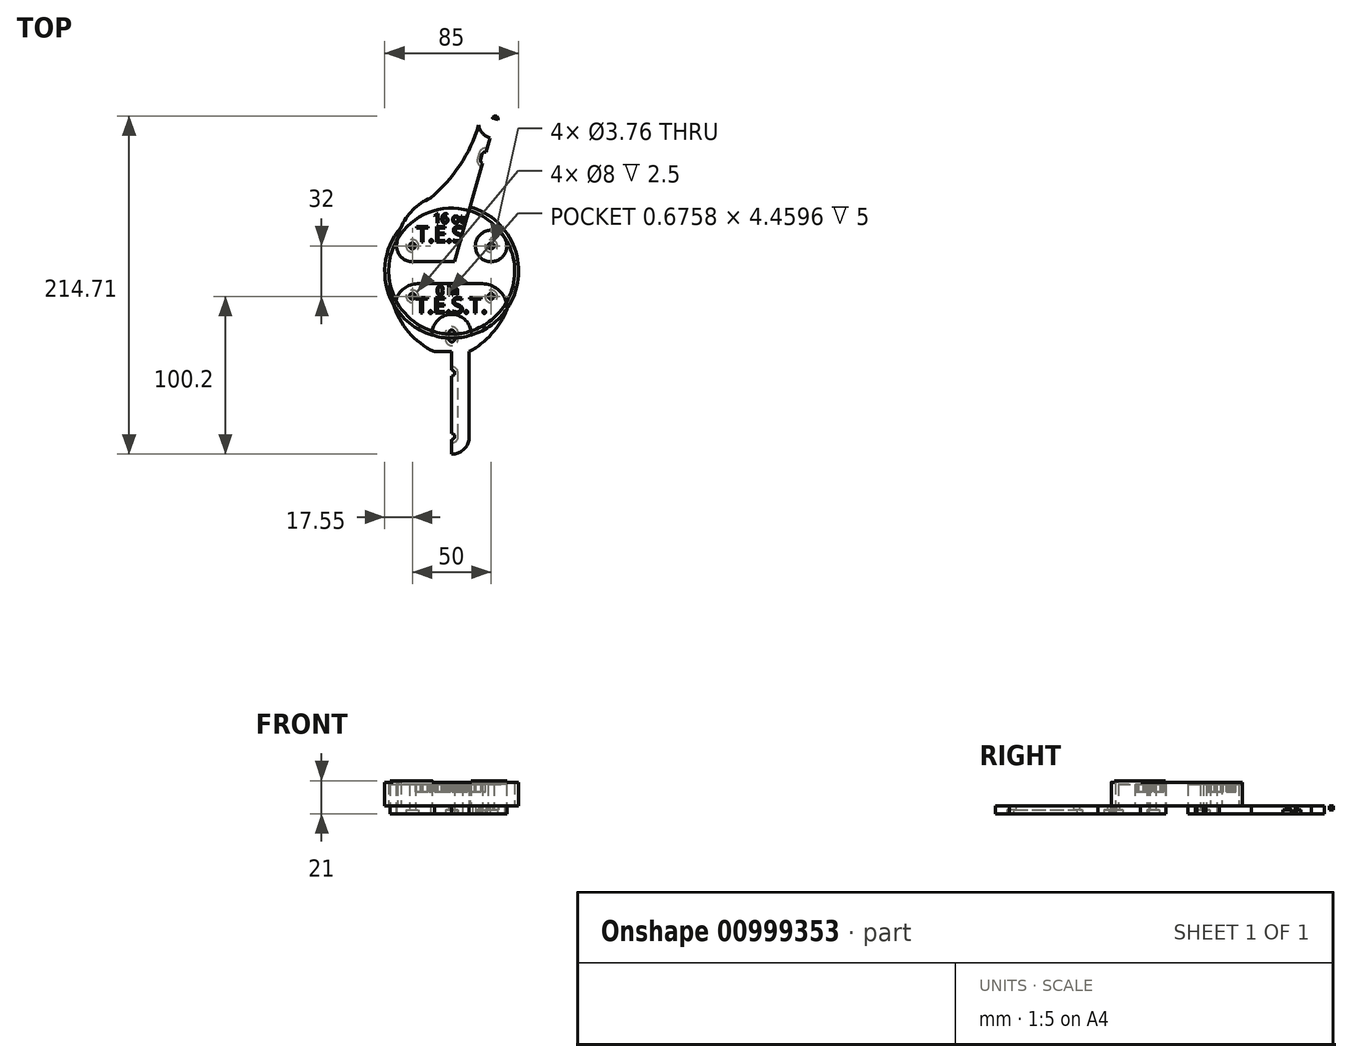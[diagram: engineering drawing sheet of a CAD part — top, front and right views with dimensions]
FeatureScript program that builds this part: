
annotation { "Feature Type Name" : "Feature", "Feature Type Description" : "" }
export const myFeature = defineFeature(function(context is Context, id is Id, definition is map)
    precondition{}
    {
        {
            var Q0;
            Q0=qCreatedBy(makeId("Top.planeOp"),FACE);
            var sketch = newSketch(context, id + "F0", { "sketchPlane" : qUnion([Q0])});
            skCircle(sketch, "E0", {"center": v(0.05, 0) * mm, "radius": 40 * mm});
            skLineSegment(sketch, "E1", {"start": v(0.05, 0) * mm, "end": v(0.05, -41.2) * mm});
            skLineSegment(sketch, "E2", {"start": v(0.05, -41.2) * mm, "end": v(0.05, -51.2) * mm});
            skLineSegment(sketch, "E3", {"start": v(0.05, -51.2) * mm, "end": v(0.05, -116.2) * mm});
            skLineSegment(sketch, "E4.bottom", {"start": v(6.4, -39.7) * mm, "end": v(-6.3, -39.7) * mm});
            skLineSegment(sketch, "E4.top", {"start": v(6.4, -42.7) * mm, "end": v(-6.3, -42.7) * mm});
            skLineSegment(sketch, "E4.left", {"start": v(6.4, -39.7) * mm, "end": v(6.4, -42.7) * mm});
            skLineSegment(sketch, "E4.right", {"start": v(-6.3, -39.7) * mm, "end": v(-6.3, -42.7) * mm});
            skPoint(sketch, "E4.middle", {"position": v(0.05, -41.2) * mm});
            skLineSegment(sketch, "E5", {"start": v(0.05, -51.2) * mm, "end": v(0.05, -83.7) * mm});
            skLineSegment(sketch, "E6.bottom", {"start": v(11.05, -51.2) * mm, "end": v(-10.95, -51.2) * mm});
            skLineSegment(sketch, "E6.top", {"start": v(11.05, -116.2) * mm, "end": v(-10.95, -116.2) * mm});
            skLineSegment(sketch, "E6.left", {"start": v(11.05, -51.2) * mm, "end": v(11.05, -107.3) * mm});
            skLineSegment(sketch, "E6.right", {"start": v(-10.95, -51.2) * mm, "end": v(-10.95, -116.2) * mm});
            skPoint(sketch, "E6.middle", {"position": v(0.05, -83.7) * mm});
            skLineSegment(sketch, "E7", {"start": v(0.05, 0) * mm, "end": v(0.05, 40) * mm});
            skLineSegment(sketch, "E8", {"start": v(0.05, 0) * mm, "end": v(27.31, 95.07) * mm});
            skLineSegment(sketch, "E9", {"start": v(0.05, 0) * mm, "end": v(20.72, 72.1) * mm});
            skLineSegment(sketch, "E10", {"start": v(20.72, 72.1) * mm, "end": v(27.31, 95.07) * mm});
            skPoint(sketch, "E11.middle", {"position": v(20.72, 72.1) * mm});
            skPoint(sketch, "E12", {"position": v(27.31, 95.07) * mm});
            skPoint(sketch, "E13.middle", {"position": v(28.16, 97.72) * mm});
            skLineSegment(sketch, "E14.1", {"start": v(-16.81, 74.6) * mm, "end": v(-16.81, 74.6) * mm});
            skCircle(sketch, "E15", {"center": v(-1, 0) * mm, "radius": 25.65 * mm});
            skLineSegment(sketch, "E16", {"start": v(0.05, 0) * mm, "end": v(0.05, -16) * mm});
            skLineSegment(sketch, "E17", {"start": v(0.05, -16) * mm, "end": v(0.05, 0) * mm});
            skLineSegment(sketch, "E18", {"start": v(0.05, 0) * mm, "end": v(0.05, 16) * mm});
            skLineSegment(sketch, "E19", {"start": v(0.05, 16) * mm, "end": v(25.05, 16) * mm});
            skLineSegment(sketch, "E20", {"start": v(0.05, -16) * mm, "end": v(-24.95, -16) * mm});
            skLineSegment(sketch, "E21", {"start": v(0.05, -16) * mm, "end": v(25.05, -16) * mm});
            skLineSegment(sketch, "E22", {"start": v(0.05, 16) * mm, "end": v(-24.95, 16) * mm});
            skCircle(sketch, "E23", {"center": v(-24.95, 16) * mm, "radius": 1.88 * mm});
            skCircle(sketch, "E24", {"center": v(25.05, 16) * mm, "radius": 1.88 * mm});
            skCircle(sketch, "E25", {"center": v(-24.95, -16) * mm, "radius": 1.88 * mm});
            skCircle(sketch, "E26", {"center": v(25.05, -16) * mm, "radius": 1.88 * mm});
            skLineSegment(sketch, "E27", {"start": v(24.44, 85.07) * mm, "end": v(27.24, 94.82) * mm});
            skCircle(sketch, "E28", {"center": v(27.24, 94.82) * mm, "radius": 1.88 * mm});
            skArc(sketch, "E29", {"start": v(18.92, 72.61) * mm, "mid": v(20.7, 70.22) * mm, "end": v(22.54, 72.55) * mm});
            skCircle(sketch, "E30", {"center": v(21.24, 73.9) * mm, "radius": 1.88 * mm});
            skCircle(sketch, "E31", {"center": v(20.2, 70.3) * mm, "radius": 1.88 * mm});
            skLineSegment(sketch, "E32", {"start": v(19.44, 74.41) * mm, "end": v(21.24, 73.9) * mm});
            skLineSegment(sketch, "E33", {"start": v(21.24, 73.9) * mm, "end": v(23.04, 73.38) * mm});
            skLineSegment(sketch, "E34", {"start": v(20.2, 70.3) * mm, "end": v(22.01, 69.78) * mm});
            skLineSegment(sketch, "E35", {"start": v(23.04, 73.38) * mm, "end": v(22.01, 69.78) * mm});
            skLineSegment(sketch, "E36", {"start": v(20.2, 70.3) * mm, "end": v(18.4, 70.8) * mm});
            skLineSegment(sketch, "E37", {"start": v(19.44, 74.41) * mm, "end": v(18.4, 70.8) * mm});
            skCircle(sketch, "E38", {"center": v(26.73, 93.02) * mm, "radius": 1.88 * mm});
            skLineSegment(sketch, "E39", {"start": v(27.24, 94.82) * mm, "end": v(27.73, 96.63) * mm});
            skCircle(sketch, "E40", {"center": v(27.73, 96.63) * mm, "radius": 1.88 * mm});
            skLineSegment(sketch, "E41", {"start": v(26.73, 93.02) * mm, "end": v(24.92, 93.54) * mm});
            skLineSegment(sketch, "E42", {"start": v(24.92, 93.54) * mm, "end": v(26.73, 93.02) * mm});
            skLineSegment(sketch, "E43", {"start": v(26.73, 93.02) * mm, "end": v(28.53, 92.5) * mm});
            skLineSegment(sketch, "E44", {"start": v(28.53, 92.5) * mm, "end": v(29.54, 96.13) * mm});
            skLineSegment(sketch, "E45", {"start": v(24.92, 93.54) * mm, "end": v(25.93, 97.14) * mm});
            skLineSegment(sketch, "E46", {"start": v(25.93, 97.14) * mm, "end": v(29.54, 96.13) * mm});
            skLineSegment(sketch, "E47", {"start": v(0.05, -8) * mm, "end": v(-39.14, -8) * mm});
            skLineSegment(sketch, "E48", {"start": v(-39.14, -8) * mm, "end": v(0.05, -8) * mm});
            skLineSegment(sketch, "E49", {"start": v(0.05, -8) * mm, "end": v(39.24, -8) * mm});
            skLineSegment(sketch, "E50", {"start": v(39.24, -8) * mm, "end": v(39.24, -38) * mm});
            skLineSegment(sketch, "E51", {"start": v(-39.14, -8) * mm, "end": v(-39.14, -38) * mm});
            skArc(sketch, "E52", {"start": v(-39.14, -8) * mm, "mid": v(-31.2, -33.61) * mm, "end": v(-10.95, -51.2) * mm});
            skArc(sketch, "E53", {"start": v(11.05, -51.2) * mm, "mid": v(30.57, -33.14) * mm, "end": v(39.24, -8) * mm});
            skArc(sketch, "E54", {"start": v(-10.95, -107.14) * mm, "mid": v(-0.02, -116.2) * mm, "end": v(11.05, -107.3) * mm});
            skCircle(sketch, "E55", {"center": v(0.05, -64.77) * mm, "radius": 1.88 * mm});
            skCircle(sketch, "E56", {"center": v(0.07, -104.97) * mm, "radius": 1.88 * mm});
            skLineSegment(sketch, "E57.bottom", {"start": v(1.93, -64.77) * mm, "end": v(-1.8, -64.77) * mm});
            skLineSegment(sketch, "E57.top", {"start": v(1.93, -104.97) * mm, "end": v(-1.8, -104.97) * mm});
            skLineSegment(sketch, "E57.left", {"start": v(1.93, -64.77) * mm, "end": v(1.93, -104.97) * mm});
            skLineSegment(sketch, "E57.right", {"start": v(-1.8, -64.77) * mm, "end": v(-1.8, -104.97) * mm});
            skCircle(sketch, "E58", {"center": v(0.05, -41.2) * mm, "radius": 1.88 * mm});
            skCircle(sketch, "E59", {"center": v(0.05, -39.32) * mm, "radius": 1.88 * mm});
            skCircle(sketch, "E60", {"center": v(0.05, -43.08) * mm, "radius": 1.88 * mm});
            skLineSegment(sketch, "E61.bottom", {"start": v(1.93, -39.25) * mm, "end": v(-1.82, -39.25) * mm});
            skLineSegment(sketch, "E61.top", {"start": v(1.93, -43.24) * mm, "end": v(-1.82, -43.24) * mm});
            skLineSegment(sketch, "E61.left", {"start": v(1.93, -39.25) * mm, "end": v(1.93, -43.24) * mm});
            skLineSegment(sketch, "E61.right", {"start": v(-1.82, -39.25) * mm, "end": v(-1.82, -43.24) * mm});
            skArc(sketch, "E62", {"start": v(-21.43, -8) * mm, "mid": v(-32.46, -13.01) * mm, "end": v(-35.8, -24.66) * mm});
            skArc(sketch, "E63", {"start": v(35.29, -24.2) * mm, "mid": v(30.8, -12.89) * mm, "end": v(19.65, -8) * mm});
            skCircle(sketch, "E64", {"center": v(-24.95, 16) * mm, "radius": 10 * mm});
            skCircle(sketch, "E65", {"center": v(25.05, 16) * mm, "radius": 10 * mm});
            skLineSegment(sketch, "E66", {"start": v(-24.95, 6) * mm, "end": v(25.05, 6) * mm});
            skCircle(sketch, "E67", {"center": v(27.08, 94.24) * mm, "radius": 10 * mm});
            skArc(sketch, "E68", {"start": v(34.09, 20.29) * mm, "mid": v(34.15, 20.55) * mm, "end": v(34.22, 20.8) * mm});
            skArc(sketch, "E69", {"start": v(-35.43, 18.48) * mm, "mid": v(-35.15, 16.05) * mm, "end": v(-34.67, 13.65) * mm});
            skArc(sketch, "E70", {"start": v(33.49, 10.63) * mm, "mid": v(33.8, 11.18) * mm, "end": v(34.1, 11.74) * mm});
            skArc(sketch, "E71", {"start": v(35.05, 16.05) * mm, "mid": v(0.05, 49.11) * mm, "end": v(-34.95, 16.05) * mm});
            skPoint(sketch, "E71.startSnap0", {"position": v(-35.15, 16.05) * mm});
            skPoint(sketch, "E71.endSnap0", {"position": v(-35.15, 16.05) * mm});
            skArc(sketch, "E72", {"start": v(-13.46, 46.4) * mm, "mid": v(5.25, 67.32) * mm, "end": v(17.2, 92.7) * mm});
            skArc(sketch, "E73", {"start": v(33.73, 86.78) * mm, "mid": v(28.6, 59.44) * mm, "end": v(30.36, 31.68) * mm});
            skPoint(sketch, "E73.endSnap0", {"position": v(27.49, 95.73) * mm});
            skArc(sketch, "E74", {"start": v(14, 83.79) * mm, "mid": v(16.02, 89.8) * mm, "end": v(17.24, 96.04) * mm});
            skArc(sketch, "E75", {"start": v(36.27, 90.32) * mm, "mid": v(33.58, 84.94) * mm, "end": v(31.61, 79.26) * mm});
            skSolve(sketch);
        }
        {
            var Q0;
            Q0=makeQuery(id+"F0.imprint","IMPRINT",FACE,{"disambiguationData":[TD([[makeQuery(id+"F0.imprint","IMPRINT",EDGE,{"derivedFrom":sQuery(id+"F0.wireOp",EDGE,"E25")}),-1.0]])]});
            var Q1;
            {var subQ0=sQuery(id+"F0.wireOp",EDGE,"E21");var subQ3=sQuery(id+"F0.wireOp",EDGE,"E15");var subQ5=makeQuery(id+"F0.imprint","INTERSECT",VERTEX,{"derivedFrom":[subQ3,subQ0]});Q1=makeQuery(id+"F0.imprint","IMPRINT",FACE,{"disambiguationData":[TD([[makeQuery(id+"F0.imprint","IMPRINT",EDGE,{"disambiguationData":[TD([[subQ5,1.0]])],"derivedFrom":subQ3}),1.0]])]});}
            var Q2;
            {var subQ0=sQuery(id+"F0.wireOp",EDGE,"E20");var subQ3=sQuery(id+"F0.wireOp",EDGE,"E15");var subQ5=makeQuery(id+"F0.imprint","INTERSECT",VERTEX,{"derivedFrom":[subQ3,subQ0]});Q2=makeQuery(id+"F0.imprint","IMPRINT",FACE,{"disambiguationData":[TD([[makeQuery(id+"F0.imprint","IMPRINT",EDGE,{"disambiguationData":[TD([[subQ5,-1.0]])],"derivedFrom":subQ3}),1.0]])]});}
            var Q3;
            {var subQ5=sQuery(id+"F0.wireOp",EDGE,"E20");var subQ7=sQuery(id+"F0.wireOp",EDGE,"E15");var subQ8=makeQuery(id+"F0.imprint","INTERSECT",VERTEX,{"derivedFrom":[subQ7,subQ5]});Q3=makeQuery(id+"F0.imprint","IMPRINT",FACE,{"disambiguationData":[TD([[makeQuery(id+"F0.imprint","IMPRINT",EDGE,{"disambiguationData":[TD([[subQ8,1.0]])],"derivedFrom":subQ7}),1.0]])]});}
            var Q4;
            {var subQ0=sQuery(id+"F0.wireOp",EDGE,"E21");var subQ3=sQuery(id+"F0.wireOp",EDGE,"E15");var subQ4=makeQuery(id+"F0.imprint","INTERSECT",VERTEX,{"derivedFrom":[subQ3,subQ0]});Q4=makeQuery(id+"F0.imprint","IMPRINT",FACE,{"disambiguationData":[TD([[makeQuery(id+"F0.imprint","IMPRINT",EDGE,{"disambiguationData":[TD([[subQ4,-1.0]])],"derivedFrom":subQ3}),1.0]])]});}
            var Q5;
            Q5=makeQuery(id+"F0.imprint","IMPRINT",FACE,{"disambiguationData":[TD([[makeQuery(id+"F0.imprint","IMPRINT",EDGE,{"derivedFrom":sQuery(id+"F0.wireOp",EDGE,"E26")}),-1.0]])]});
            var Q6;
            {var subQ15=sQuery(id+"F0.wireOp",EDGE,"E4.left");Q6=makeQuery(id+"F0.imprint","IMPRINT",FACE,{"disambiguationData":[TD([[makeQuery(id+"F0.imprint","IMPRINT",EDGE,{"derivedFrom":subQ15}),1.0]])]});}
            var Q7;
            {var subQ14=sQuery(id+"F0.wireOp",EDGE,"E4.right");Q7=makeQuery(id+"F0.imprint","IMPRINT",FACE,{"disambiguationData":[TD([[makeQuery(id+"F0.imprint","IMPRINT",EDGE,{"derivedFrom":subQ14}),-1.0]])]});}
            var Q8;
            {var subQ0=sQuery(id+"F0.wireOp",EDGE,"E4.right");Q8=makeQuery(id+"F0.imprint","IMPRINT",FACE,{"disambiguationData":[TD([[makeQuery(id+"F0.imprint","IMPRINT",EDGE,{"derivedFrom":subQ0}),1.0]])]});}
            var Q9;
            {var subQ0=sQuery(id+"F0.wireOp",EDGE,"E4.left");Q9=makeQuery(id+"F0.imprint","IMPRINT",FACE,{"disambiguationData":[TD([[makeQuery(id+"F0.imprint","IMPRINT",EDGE,{"derivedFrom":subQ0}),-1.0]])]});}
            var Q10;
            {var subQ0=sQuery(id+"F0.wireOp",EDGE,"E6.left");Q10=makeQuery(id+"F0.imprint","IMPRINT",FACE,{"disambiguationData":[TD([[makeQuery(id+"F0.imprint","IMPRINT",EDGE,{"derivedFrom":subQ0}),-1.0]])]});}
            var Q11;
            {var subQ8=sQuery(id+"F0.wireOp",EDGE,"E55");var subQ10=sQuery(id+"F0.wireOp",EDGE,"E5");var subQ12=makeQuery(id+"F0.imprint","INTERSECT",VERTEX,{"disambiguationData":[OD(0.0)],"derivedFrom":[subQ10,subQ8]});Q11=makeQuery(id+"F0.imprint","IMPRINT",FACE,{"disambiguationData":[TD([[makeQuery(id+"F0.imprint","IMPRINT",EDGE,{"disambiguationData":[TD([[subQ12,-1.0]])],"derivedFrom":subQ8}),-1.0]])]});}
            var Q12;
            {var subQ0=sQuery(id+"F0.wireOp",EDGE,"E22");var subQ1=sQuery(id+"F0.wireOp",EDGE,"E15");var subQ2=makeQuery(id+"F0.imprint","INTERSECT",VERTEX,{"derivedFrom":[subQ1,subQ0]});Q12=makeQuery(id+"F0.imprint","IMPRINT",FACE,{"disambiguationData":[TD([[makeQuery(id+"F0.imprint","IMPRINT",EDGE,{"disambiguationData":[TD([[subQ2,-1.0]])],"derivedFrom":subQ1}),1.0]])]});}
            var Q13;
            {var subQ3=sQuery(id+"F0.wireOp",EDGE,"E66");var subQ5=sQuery(id+"F0.wireOp",EDGE,"E64");var subQ7=makeQuery(id+"F0.imprint","INTERSECT",VERTEX,{"derivedFrom":[subQ5,subQ3]});Q13=makeQuery(id+"F0.imprint","IMPRINT",FACE,{"disambiguationData":[TD([[makeQuery(id+"F0.imprint","IMPRINT",EDGE,{"disambiguationData":[TD([[subQ7,-1.0]])],"derivedFrom":subQ5}),-1.0]])]});}
            var Q14;
            {var subQ0=sQuery(id+"F0.wireOp",EDGE,"E66");var subQ1=sQuery(id+"F0.wireOp",EDGE,"E9");var subQ2=makeQuery(id+"F0.imprint","INTERSECT",VERTEX,{"derivedFrom":[subQ1,subQ0]});Q14=makeQuery(id+"F0.imprint","IMPRINT",FACE,{"disambiguationData":[TD([[makeQuery(id+"F0.imprint","IMPRINT",EDGE,{"disambiguationData":[TD([[subQ2,-1.0]])],"derivedFrom":subQ1}),1.0]])]});}
            var Q15;
            {var subQ5=sQuery(id+"F0.wireOp",EDGE,"E9");var subQ7=sQuery(id+"F0.wireOp",EDGE,"E66");var subQ9=makeQuery(id+"F0.imprint","INTERSECT",VERTEX,{"derivedFrom":[subQ5,subQ7]});Q15=makeQuery(id+"F0.imprint","IMPRINT",FACE,{"disambiguationData":[TD([[makeQuery(id+"F0.imprint","IMPRINT",EDGE,{"disambiguationData":[TD([[subQ9,-1.0]])],"derivedFrom":subQ5}),-1.0]])]});}
            var Q16;
            {var subQ0=sQuery(id+"F0.wireOp",EDGE,"E19");var subQ1=sQuery(id+"F0.wireOp",EDGE,"E15");var subQ2=makeQuery(id+"F0.imprint","INTERSECT",VERTEX,{"derivedFrom":[subQ1,subQ0]});Q16=makeQuery(id+"F0.imprint","IMPRINT",FACE,{"disambiguationData":[TD([[makeQuery(id+"F0.imprint","IMPRINT",EDGE,{"disambiguationData":[TD([[subQ2,1.0]])],"derivedFrom":subQ1}),1.0]])]});}
            var Q17;
            Q17=makeQuery(id+"F0.imprint","IMPRINT",FACE,{"disambiguationData":[TD([[makeQuery(id+"F0.imprint","IMPRINT",EDGE,{"derivedFrom":sQuery(id+"F0.wireOp",EDGE,"E24")}),-1.0]])]});
            var Q18;
            {var subQ0=sQuery(id+"F0.wireOp",EDGE,"E19");var subQ1=sQuery(id+"F0.wireOp",EDGE,"E9");var subQ2=makeQuery(id+"F0.imprint","INTERSECT",VERTEX,{"derivedFrom":[subQ1,subQ0]});Q18=makeQuery(id+"F0.imprint","IMPRINT",FACE,{"disambiguationData":[TD([[makeQuery(id+"F0.imprint","IMPRINT",EDGE,{"disambiguationData":[TD([[subQ2,-1.0]])],"derivedFrom":subQ1}),-1.0]])]});}
            var Q19;
            {var subQ0=sQuery(id+"F0.wireOp",EDGE,"E19");var subQ5=sQuery(id+"F0.wireOp",EDGE,"E9");var subQ6=makeQuery(id+"F0.imprint","INTERSECT",VERTEX,{"derivedFrom":[subQ5,subQ0]});Q19=makeQuery(id+"F0.imprint","IMPRINT",FACE,{"disambiguationData":[TD([[makeQuery(id+"F0.imprint","IMPRINT",EDGE,{"disambiguationData":[TD([[subQ6,-1.0]])],"derivedFrom":subQ5}),1.0]])]});}
            var Q20;
            {var subQ1=sQuery(id+"F0.wireOp",EDGE,"E7");var subQ3=sQuery(id+"F0.wireOp",EDGE,"E15");var subQ4=makeQuery(id+"F0.imprint","INTERSECT",VERTEX,{"derivedFrom":[subQ1,subQ3]});Q20=makeQuery(id+"F0.imprint","IMPRINT",FACE,{"disambiguationData":[TD([[makeQuery(id+"F0.imprint","IMPRINT",EDGE,{"disambiguationData":[TD([[subQ4,-1.0]])],"derivedFrom":subQ3}),1.0]])]});}
            var Q21;
            Q21=makeQuery(id+"F0.imprint","IMPRINT",FACE,{"disambiguationData":[TD([[makeQuery(id+"F0.imprint","IMPRINT",EDGE,{"derivedFrom":sQuery(id+"F0.wireOp",EDGE,"E23")}),-1.0]])]});
            var Q22;
            {var subQ5=sQuery(id+"F0.wireOp",EDGE,"E7");var subQ6=sQuery(id+"F0.wireOp",EDGE,"E0");var subQ7=makeQuery(id+"F0.imprint","INTERSECT",VERTEX,{"derivedFrom":[subQ6,subQ5]});Q22=makeQuery(id+"F0.imprint","IMPRINT",FACE,{"disambiguationData":[TD([[makeQuery(id+"F0.imprint","IMPRINT",EDGE,{"disambiguationData":[TD([[subQ7,-1.0]])],"derivedFrom":subQ6}),1.0]])]});}
            var Q23;
            {var subQ1=sQuery(id+"F0.wireOp",EDGE,"E0");var subQ5=makeQuery(id+"F0.imprint","INTERSECT",VERTEX,{"derivedFrom":[subQ1,sQuery(id+"F0.wireOp",EDGE,"E68")]});Q23=makeQuery(id+"F0.imprint","IMPRINT",FACE,{"disambiguationData":[TD([[makeQuery(id+"F0.imprint","IMPRINT",EDGE,{"disambiguationData":[TD([[subQ5,1.0]])],"derivedFrom":subQ1}),-1.0]])]});}
            var Q24;
            {var subQ13=sQuery(id+"F0.wireOp",EDGE,"E71");var subQ15=sQuery(id+"F0.wireOp",EDGE,"E9");var subQ16=makeQuery(id+"F0.imprint","INTERSECT",VERTEX,{"derivedFrom":[subQ15,subQ13]});Q24=makeQuery(id+"F0.imprint","IMPRINT",FACE,{"disambiguationData":[TD([[makeQuery(id+"F0.imprint","IMPRINT",EDGE,{"disambiguationData":[TD([[subQ16,-1.0]])],"derivedFrom":subQ15}),-1.0]])]});}
            var Q25;
            {var subQ11=sQuery(id+"F0.wireOp",EDGE,"E71");var subQ12=sQuery(id+"F0.wireOp",EDGE,"E9");var subQ13=makeQuery(id+"F0.imprint","INTERSECT",VERTEX,{"derivedFrom":[subQ12,subQ11]});Q25=makeQuery(id+"F0.imprint","IMPRINT",FACE,{"disambiguationData":[TD([[makeQuery(id+"F0.imprint","IMPRINT",EDGE,{"disambiguationData":[TD([[subQ13,-1.0]])],"derivedFrom":subQ12}),1.0]])]});}
            var Q26;
            {var subQ0=sQuery(id+"F0.wireOp",EDGE,"E22");var subQ1=sQuery(id+"F0.wireOp",EDGE,"E15");var subQ2=makeQuery(id+"F0.imprint","INTERSECT",VERTEX,{"derivedFrom":[subQ1,subQ0]});Q26=makeQuery(id+"F0.imprint","IMPRINT",FACE,{"disambiguationData":[TD([[makeQuery(id+"F0.imprint","IMPRINT",EDGE,{"disambiguationData":[TD([[subQ2,1.0]])],"derivedFrom":subQ1}),1.0]])]});}
            var Q27;
            {var subQ0=sQuery(id+"F0.wireOp",EDGE,"E19");var subQ1=sQuery(id+"F0.wireOp",EDGE,"E15");var subQ2=makeQuery(id+"F0.imprint","INTERSECT",VERTEX,{"derivedFrom":[subQ1,subQ0]});Q27=makeQuery(id+"F0.imprint","IMPRINT",FACE,{"disambiguationData":[TD([[makeQuery(id+"F0.imprint","IMPRINT",EDGE,{"disambiguationData":[TD([[subQ2,-1.0]])],"derivedFrom":subQ1}),1.0]])]});}
            var Q28;
            {var subQ0=sQuery(id+"F0.wireOp",EDGE,"E7");var subQ1=sQuery(id+"F0.wireOp",EDGE,"E0");var subQ2=makeQuery(id+"F0.imprint","INTERSECT",VERTEX,{"derivedFrom":[subQ1,subQ0]});Q28=makeQuery(id+"F0.imprint","IMPRINT",FACE,{"disambiguationData":[TD([[makeQuery(id+"F0.imprint","IMPRINT",EDGE,{"disambiguationData":[TD([[subQ2,1.0]])],"derivedFrom":subQ1}),1.0]])]});}
            var Q29;
            {var subQ0=sQuery(id+"F0.wireOp",EDGE,"E68");Q29=makeQuery(id+"F0.imprint","IMPRINT",FACE,{"disambiguationData":[TD([[makeQuery(id+"F0.imprint","IMPRINT",EDGE,{"derivedFrom":subQ0}),1.0]])]});}
            var Q30;
            {var subQ5=sQuery(id+"F0.wireOp",EDGE,"E45");Q30=makeQuery(id+"F0.imprint","IMPRINT",FACE,{"disambiguationData":[TD([[makeQuery(id+"F0.imprint","IMPRINT",EDGE,{"derivedFrom":subQ5}),1.0]])]});}
            var Q31;
            {var subQ1=sQuery(id+"F0.wireOp",EDGE,"E0");var subQ5=makeQuery(id+"F0.imprint","INTERSECT",VERTEX,{"derivedFrom":[subQ1,sQuery(id+"F0.wireOp",EDGE,"E7")]});Q31=makeQuery(id+"F0.imprint","IMPRINT",FACE,{"disambiguationData":[TD([[makeQuery(id+"F0.imprint","IMPRINT",EDGE,{"disambiguationData":[TD([[subQ5,1.0]])],"derivedFrom":subQ1}),-1.0]])]});}
            var Q32;
            {var subQ0=sQuery(id+"F0.wireOp",EDGE,"E68");Q32=makeQuery(id+"F0.imprint","IMPRINT",FACE,{"disambiguationData":[TD([[makeQuery(id+"F0.imprint","IMPRINT",EDGE,{"derivedFrom":subQ0}),-1.0]])]});}
            var Q33;
            {var subQ0=sQuery(id+"F0.wireOp",EDGE,"E61.left");var subQ1=sQuery(id+"F0.wireOp",EDGE,"E0");var subQ2=makeQuery(id+"F0.imprint","INTERSECT",VERTEX,{"derivedFrom":[subQ1,subQ0]});Q33=makeQuery(id+"F0.imprint","IMPRINT",FACE,{"disambiguationData":[TD([[makeQuery(id+"F0.imprint","IMPRINT",EDGE,{"disambiguationData":[TD([[subQ2,-1.0]])],"derivedFrom":subQ1}),1.0]])]});}
            var Q34;
            {var subQ0=sQuery(id+"F0.wireOp",EDGE,"E4.bottom");var subQ1=sQuery(id+"F0.wireOp",EDGE,"E0");var subQ2=makeQuery(id+"F0.imprint","INTERSECT",VERTEX,{"disambiguationData":[OD(0.0)],"derivedFrom":[subQ1,subQ0]});Q34=makeQuery(id+"F0.imprint","IMPRINT",FACE,{"disambiguationData":[TD([[makeQuery(id+"F0.imprint","IMPRINT",EDGE,{"disambiguationData":[TD([[subQ2,-1.0]])],"derivedFrom":subQ1}),1.0]])]});}
            extrude(context, id + "F1", {"entities" : qUnion([Q0, Q1, Q2, Q3, Q4, Q5, Q6, Q7, Q8, Q9, Q10, Q11, Q12, Q13, Q14, Q15, Q16, Q17, Q18, Q19, Q20, Q21, Q22, Q23, Q24, Q25, Q26, Q27, Q28, Q29, Q30, Q31, Q32, Q33, Q34]), "depth" : 5 * mm, "offsetDistance" : 25 * mm});
        }
        {
            var Q0;
            Q0=makeQuery(id+"F1.opExtrude","CAP_FACE",FACE,{"disambiguationData":[OSD([sQuery(id+"F0.wireOp",EDGE,"E6.left"),sQuery(id+"F0.wireOp",EDGE,"E6.right"),sQuery(id+"F0.wireOp",EDGE,"E25"),sQuery(id+"F0.wireOp",EDGE,"E26"),sQuery(id+"F0.wireOp",EDGE,"E48"),sQuery(id+"F0.wireOp",EDGE,"E49"),sQuery(id+"F0.wireOp",EDGE,"E52"),sQuery(id+"F0.wireOp",EDGE,"E53"),sQuery(id+"F0.wireOp",EDGE,"E54"),sQuery(id+"F0.wireOp",EDGE,"E55"),sQuery(id+"F0.wireOp",EDGE,"E56"),sQuery(id+"F0.wireOp",EDGE,"E57.left"),sQuery(id+"F0.wireOp",EDGE,"E57.right"),sQuery(id+"F0.wireOp",EDGE,"E58"),sQuery(id+"F0.wireOp",EDGE,"E59"),sQuery(id+"F0.wireOp",EDGE,"E60"),sQuery(id+"F0.wireOp",EDGE,"E61.top"),sQuery(id+"F0.wireOp",EDGE,"E61.left"),sQuery(id+"F0.wireOp",EDGE,"E61.right"),sQuery(id+"F0.wireOp",EDGE,"E62"),sQuery(id+"F0.wireOp",EDGE,"E63")])],"isStart":false});
            var sketch = newSketch(context, id + "F2", { "sketchPlane" : qUnion([Q0])});
            skCircle(sketch, "E76", {"center": v(0, 0) * mm, "radius": 40 * mm});
            skCircle(sketch, "E77", {"center": v(0, -40) * mm, "radius": 12.5 * mm});
            skCircle(sketch, "E78", {"center": v(0, 0) * mm, "radius": 42.5 * mm});
            skSolve(sketch);
        }
        {
            var Q0;
            Q0=makeQuery(id+"F2.imprint","IMPRINT",FACE,{"disambiguationData":[TD([[makeQuery(id+"F2.imprint","IMPRINT",EDGE,{"derivedFrom":makeQuery(id+"F1.opExtrude","CAP_EDGE",EDGE,{"disambiguationData":[OSD([sQuery(id+"F0.wireOp",EDGE,"E25")])],"isStart":false})}),-1.0]])]});
            extrude(context, id + "F3", {"entities" : qUnion([Q0]), "operationType" : NewBodyOperationType.ADD, "depth" : 13.8 * mm, "offsetDistance" : 25 * mm});
        }
        {
            var Q0;
            {var subQ0=sQuery(id+"F2.wireOp",EDGE,"E77");var subQ1=sQuery(id+"F2.wireOp",EDGE,"E76");var subQ2=makeQuery(id+"F2.imprint","INTERSECT",VERTEX,{"disambiguationData":[OD(0.0)],"derivedFrom":[subQ1,subQ0]});Q0=makeQuery(id+"F2.imprint","IMPRINT",FACE,{"disambiguationData":[TD([[makeQuery(id+"F2.imprint","IMPRINT",EDGE,{"disambiguationData":[TD([[subQ2,1.0]])],"derivedFrom":subQ1}),-1.0]])]});}
            var Q1;
            {var subQ0=sQuery(id+"F2.wireOp",EDGE,"E77");var subQ1=sQuery(id+"F2.wireOp",EDGE,"E76");var subQ2=makeQuery(id+"F2.imprint","INTERSECT",VERTEX,{"disambiguationData":[OD(1.0)],"derivedFrom":[subQ1,subQ0]});Q1=makeQuery(id+"F2.imprint","IMPRINT",FACE,{"disambiguationData":[TD([[makeQuery(id+"F2.imprint","IMPRINT",EDGE,{"disambiguationData":[TD([[subQ2,-1.0]])],"derivedFrom":subQ1}),-1.0]])]});}
            extrude(context, id + "F4", {"entities" : qUnion([Q0, Q1]), "operationType" : NewBodyOperationType.ADD, "depth" : 16 * mm, "offsetDistance" : 25 * mm});
        }
        {
            var Q0;
            Q0=makeQuery(id+"F1.opExtrude","CAP_FACE",FACE,{"disambiguationData":[OSD([sQuery(id+"F0.wireOp",EDGE,"E6.left"),sQuery(id+"F0.wireOp",EDGE,"E6.right"),sQuery(id+"F0.wireOp",EDGE,"E25"),sQuery(id+"F0.wireOp",EDGE,"E26"),sQuery(id+"F0.wireOp",EDGE,"E48"),sQuery(id+"F0.wireOp",EDGE,"E49"),sQuery(id+"F0.wireOp",EDGE,"E52"),sQuery(id+"F0.wireOp",EDGE,"E53"),sQuery(id+"F0.wireOp",EDGE,"E54"),sQuery(id+"F0.wireOp",EDGE,"E55"),sQuery(id+"F0.wireOp",EDGE,"E56"),sQuery(id+"F0.wireOp",EDGE,"E57.left"),sQuery(id+"F0.wireOp",EDGE,"E57.right"),sQuery(id+"F0.wireOp",EDGE,"E58"),sQuery(id+"F0.wireOp",EDGE,"E59"),sQuery(id+"F0.wireOp",EDGE,"E60"),sQuery(id+"F0.wireOp",EDGE,"E61.top"),sQuery(id+"F0.wireOp",EDGE,"E61.left"),sQuery(id+"F0.wireOp",EDGE,"E61.right"),sQuery(id+"F0.wireOp",EDGE,"E62"),sQuery(id+"F0.wireOp",EDGE,"E63")])],"isStart":true});
            var sketch = newSketch(context, id + "F5", { "sketchPlane" : qUnion([Q0])});
            skCircle(sketch, "E79", {"center": v(-24.95, 16) * mm, "radius": 4 * mm});
            skCircle(sketch, "E80", {"center": v(25.05, 16) * mm, "radius": 4 * mm});
            skCircle(sketch, "E81", {"center": v(0.05, 39.32) * mm, "radius": 4 * mm});
            skCircle(sketch, "E82", {"center": v(0, 43.24) * mm, "radius": 4 * mm});
            skCircle(sketch, "E83", {"center": v(0.05, 64.77) * mm, "radius": 4 * mm});
            skCircle(sketch, "E84", {"center": v(0.2, 104.97) * mm, "radius": 4 * mm});
            skPoint(sketch, "E84.centerSnap0", {"position": v(0.2, 106.84) * mm});
            skLineSegment(sketch, "E85.bottom", {"start": v(4.18, 105.33) * mm, "end": v(-3.92, 105.33) * mm});
            skLineSegment(sketch, "E85.top", {"start": v(4.18, 64.34) * mm, "end": v(-3.92, 64.34) * mm});
            skLineSegment(sketch, "E85.left", {"start": v(4.18, 105.33) * mm, "end": v(4.18, 64.34) * mm});
            skLineSegment(sketch, "E85.right", {"start": v(-3.92, 105.33) * mm, "end": v(-3.92, 64.34) * mm});
            skLineSegment(sketch, "E86.bottom", {"start": v(-3.92, 38.86) * mm, "end": v(3.93, 38.86) * mm});
            skLineSegment(sketch, "E86.top", {"start": v(-3.92, 44) * mm, "end": v(3.93, 44) * mm});
            skLineSegment(sketch, "E86.left", {"start": v(-3.92, 38.86) * mm, "end": v(-3.92, 44) * mm});
            skLineSegment(sketch, "E86.right", {"start": v(3.93, 38.86) * mm, "end": v(3.93, 44) * mm});
            skSolve(sketch);
        }
        {
            var Q0;
            Q0 = qSketchRegion(id + "F5", true);
            var Q1;
            {var subQ0=sQuery(id+"F0.wireOp",EDGE,"E61.right");var subQ2=sQuery(id+"F0.wireOp",EDGE,"E58");var subQ3=makeQuery(id+"F0.imprint","INTERSECT",VERTEX,{"disambiguationData":[OD(0.0)],"derivedFrom":[subQ2,subQ0]});var subQ7=makeQuery(id+"F1.opExtrude","CAP_EDGE",EDGE,{"disambiguationData":[OSD([subQ2]),TDD([makeQuery(id+"F0.imprint","IMPRINT",EDGE,{"disambiguationData":[TD([[subQ3,-1.0]])],"derivedFrom":subQ2})])],"isStart":true});Q1=makeQuery(id+"F5.imprint","IMPRINT",FACE,{"disambiguationData":[TD([[makeQuery(id+"F5.imprint","IMPRINT",EDGE,{"derivedFrom":subQ7}),1.0]])]});}
            var Q2;
            {var subQ0=sQuery(id+"F0.wireOp",EDGE,"E61.left");var subQ1=sQuery(id+"F0.wireOp",EDGE,"E58");var subQ2=makeQuery(id+"F0.imprint","INTERSECT",VERTEX,{"disambiguationData":[OD(0.0)],"derivedFrom":[subQ1,subQ0]});var subQ4=makeQuery(id+"F1.opExtrude","CAP_EDGE",EDGE,{"disambiguationData":[OSD([subQ1]),TDD([makeQuery(id+"F0.imprint","IMPRINT",EDGE,{"disambiguationData":[TD([[subQ2,1.0]])],"derivedFrom":subQ1})])],"isStart":true});Q2=makeQuery(id+"F5.imprint","IMPRINT",FACE,{"disambiguationData":[TD([[makeQuery(id+"F5.imprint","IMPRINT",EDGE,{"derivedFrom":subQ4}),1.0]])]});}
            extrude(context, id + "F6", {"entities" : qUnion([Q0, Q1, Q2]), "operationType" : NewBodyOperationType.REMOVE, "oppositeDirection" : true, "depth" : 2.5 * mm, "offsetDistance" : 25 * mm});
        }
        {
            var Q0;
            Q0=makeQuery(id+"F1.opExtrude","CAP_FACE",FACE,{"disambiguationData":[OSD([sQuery(id+"F0.wireOp",EDGE,"E15"),sQuery(id+"F0.wireOp",EDGE,"E23"),sQuery(id+"F0.wireOp",EDGE,"E24"),sQuery(id+"F0.wireOp",EDGE,"E28"),sQuery(id+"F0.wireOp",EDGE,"E30"),sQuery(id+"F0.wireOp",EDGE,"E31"),sQuery(id+"F0.wireOp",EDGE,"E35"),sQuery(id+"F0.wireOp",EDGE,"E37"),sQuery(id+"F0.wireOp",EDGE,"E38"),sQuery(id+"F0.wireOp",EDGE,"E40"),sQuery(id+"F0.wireOp",EDGE,"E44"),sQuery(id+"F0.wireOp",EDGE,"E45"),sQuery(id+"F0.wireOp",EDGE,"E64"),sQuery(id+"F0.wireOp",EDGE,"E65"),sQuery(id+"F0.wireOp",EDGE,"E66"),sQuery(id+"F0.wireOp",EDGE,"E67"),sQuery(id+"F0.wireOp",EDGE,"7zZgwB8g-Wi2Y-ta59-iiN9-ImOjuoIbdOXE"),sQuery(id+"F0.wireOp",EDGE,"2vqOZzAz-xV0X-aR0t-WXtd-OeHWlmNv4bZk"),sQuery(id+"F0.wireOp",EDGE,"QdtOUSRX-a4rU-OEUg-KCwG-PbmQteqAubiP"),sQuery(id+"F0.wireOp",EDGE,"E69"),sQuery(id+"F0.wireOp",EDGE,"agruSzEX-hiuo-YuLb-t9cE-62ZsMYZAz0FI"),sQuery(id+"F0.wireOp",EDGE,"E70"),sQuery(id+"F0.wireOp",EDGE,"0vQUtCWi-EhDK-WcMH-Y7Eb-2PAa2n6cAjc3")])],"isStart":false});
            var sketch = newSketch(context, id + "F7", { "sketchPlane" : qUnion([Q0])});
            skCircle(sketch, "E87", {"center": v(0, 0) * mm, "radius": 40 * mm});
            skCircle(sketch, "E88", {"center": v(0, 0) * mm, "radius": 42.5 * mm});
            skSolve(sketch);
        }
        {
            var Q0;
            Q0=makeQuery(id+"F7.imprint","IMPRINT",FACE,{"disambiguationData":[TD([[makeQuery(id+"F7.imprint","IMPRINT",EDGE,{"derivedFrom":makeQuery(id+"F1.opExtrude","CAP_EDGE",EDGE,{"disambiguationData":[OSD([sQuery(id+"F0.wireOp",EDGE,"E15")])],"isStart":false})}),1.0]])]});
            extrude(context, id + "F8", {"entities" : qUnion([Q0]), "operationType" : NewBodyOperationType.ADD, "depth" : 13.8 * mm, "offsetDistance" : 25 * mm});
        }
        {
            var Q0;
            Q0=makeQuery(id+"F1.opExtrude","CAP_FACE",FACE,{"disambiguationData":[OSD([sQuery(id+"F0.wireOp",EDGE,"E15"),sQuery(id+"F0.wireOp",EDGE,"E23"),sQuery(id+"F0.wireOp",EDGE,"E24"),sQuery(id+"F0.wireOp",EDGE,"E28"),sQuery(id+"F0.wireOp",EDGE,"E30"),sQuery(id+"F0.wireOp",EDGE,"E31"),sQuery(id+"F0.wireOp",EDGE,"E35"),sQuery(id+"F0.wireOp",EDGE,"E37"),sQuery(id+"F0.wireOp",EDGE,"E38"),sQuery(id+"F0.wireOp",EDGE,"E40"),sQuery(id+"F0.wireOp",EDGE,"E44"),sQuery(id+"F0.wireOp",EDGE,"E45"),sQuery(id+"F0.wireOp",EDGE,"E64"),sQuery(id+"F0.wireOp",EDGE,"E65"),sQuery(id+"F0.wireOp",EDGE,"E66"),sQuery(id+"F0.wireOp",EDGE,"E67"),sQuery(id+"F0.wireOp",EDGE,"7zZgwB8g-Wi2Y-ta59-iiN9-ImOjuoIbdOXE"),sQuery(id+"F0.wireOp",EDGE,"2vqOZzAz-xV0X-aR0t-WXtd-OeHWlmNv4bZk"),sQuery(id+"F0.wireOp",EDGE,"QdtOUSRX-a4rU-OEUg-KCwG-PbmQteqAubiP"),sQuery(id+"F0.wireOp",EDGE,"E69"),sQuery(id+"F0.wireOp",EDGE,"agruSzEX-hiuo-YuLb-t9cE-62ZsMYZAz0FI"),sQuery(id+"F0.wireOp",EDGE,"E70"),sQuery(id+"F0.wireOp",EDGE,"0vQUtCWi-EhDK-WcMH-Y7Eb-2PAa2n6cAjc3")])],"isStart":true});
            var sketch = newSketch(context, id + "F9", { "sketchPlane" : qUnion([Q0])});
            skCircle(sketch, "E89", {"center": v(25.05, -16) * mm, "radius": 4 * mm});
            skCircle(sketch, "E90", {"center": v(-24.95, -16) * mm, "radius": 4 * mm});
            skCircle(sketch, "E91", {"center": v(20.2, -70.3) * mm, "radius": 4 * mm});
            skCircle(sketch, "E92", {"center": v(21.4, -74.11) * mm, "radius": 4 * mm});
            skCircle(sketch, "E93", {"center": v(27.73, -96.63) * mm, "radius": 4 * mm});
            skCircle(sketch, "E94", {"center": v(26.73, -93.02) * mm, "radius": 4 * mm});
            skLineSegment(sketch, "E95", {"start": v(31.68, -96.02) * mm, "end": v(30.37, -91.37) * mm});
            skLineSegment(sketch, "E96", {"start": v(24.1, -98.3) * mm, "end": v(22.77, -93.63) * mm});
            skLineSegment(sketch, "E97", {"start": v(17.72, -75.7) * mm, "end": v(16.4, -71.5) * mm});
            skPoint(sketch, "E97.startSnap0", {"position": v(21.76, -75.7) * mm});
            skLineSegment(sketch, "E98", {"start": v(16.4, -71.5) * mm, "end": v(25.33, -73.38) * mm});
            skLineSegment(sketch, "E99", {"start": v(25.33, -73.38) * mm, "end": v(24.04, -69.13) * mm});
            skSolve(sketch);
        }
        {
            var Q0;
            Q0 = qSketchRegion(id + "F9", true);
            var Q1;
            {var subQ0=sQuery(id+"F9.wireOp",EDGE,"E92");var subQ1=sQuery(id+"F9.wireOp",EDGE,"E91");var subQ2=makeQuery(id+"F9.imprint","INTERSECT",VERTEX,{"disambiguationData":[OD(0.0)],"derivedFrom":[subQ1,subQ0]});Q1=makeQuery(id+"F9.imprint","IMPRINT",FACE,{"disambiguationData":[TD([[makeQuery(id+"F9.imprint","IMPRINT",EDGE,{"disambiguationData":[TD([[subQ2,-1.0]])],"derivedFrom":subQ1}),1.0]])]});}
            var Q2;
            {var subQ0=sQuery(id+"F9.wireOp",EDGE,"E98");var subQ1=sQuery(id+"F9.wireOp",EDGE,"E92");var subQ2=makeQuery(id+"F9.imprint","INTERSECT",VERTEX,{"derivedFrom":[subQ1,subQ0]});Q2=makeQuery(id+"F9.imprint","IMPRINT",FACE,{"disambiguationData":[TD([[makeQuery(id+"F9.imprint","IMPRINT",EDGE,{"disambiguationData":[TD([[subQ2,1.0]])],"derivedFrom":subQ1}),1.0]])]});}
            var Q3;
            {var subQ0=sQuery(id+"F9.wireOp",EDGE,"E98");var subQ1=sQuery(id+"F9.wireOp",EDGE,"E91");var subQ2=makeQuery(id+"F9.imprint","INTERSECT",VERTEX,{"derivedFrom":[subQ1,subQ0]});Q3=makeQuery(id+"F9.imprint","IMPRINT",FACE,{"disambiguationData":[TD([[makeQuery(id+"F9.imprint","IMPRINT",EDGE,{"disambiguationData":[TD([[subQ2,-1.0]])],"derivedFrom":subQ1}),1.0]])]});}
            var Q4;
            {var subQ1=sQuery(id+"F0.wireOp",EDGE,"E28");var subQ3=makeQuery(id+"F1.opExtrude","CAP_EDGE",EDGE,{"disambiguationData":[OSD([subQ1])],"isStart":true});Q4=makeQuery(id+"F9.imprint","IMPRINT",FACE,{"disambiguationData":[TD([[makeQuery(id+"F9.imprint","IMPRINT",EDGE,{"derivedFrom":subQ3}),1.0]])]});}
            var Q5;
            {var subQ0=sQuery(id+"F9.wireOp",EDGE,"E94");var subQ1=sQuery(id+"F9.wireOp",EDGE,"E93");var subQ2=makeQuery(id+"F9.imprint","INTERSECT",VERTEX,{"disambiguationData":[OD(1.0)],"derivedFrom":[subQ1,subQ0]});Q5=makeQuery(id+"F9.imprint","IMPRINT",FACE,{"disambiguationData":[TD([[makeQuery(id+"F9.imprint","IMPRINT",EDGE,{"disambiguationData":[TD([[subQ2,1.0]])],"derivedFrom":subQ1}),1.0]])]});}
            var Q6;
            {var subQ0=sQuery(id+"F9.wireOp",EDGE,"E98");var subQ1=sQuery(id+"F9.wireOp",EDGE,"E91");var subQ2=makeQuery(id+"F9.imprint","INTERSECT",VERTEX,{"derivedFrom":[subQ1,subQ0]});Q6=makeQuery(id+"F9.imprint","IMPRINT",FACE,{"disambiguationData":[TD([[makeQuery(id+"F9.imprint","IMPRINT",EDGE,{"disambiguationData":[TD([[subQ2,1.0]])],"derivedFrom":subQ1}),1.0]])]});}
            extrude(context, id + "F10", {"entities" : qUnion([Q0, Q1, Q2, Q3, Q4, Q5, Q6]), "operationType" : NewBodyOperationType.REMOVE, "oppositeDirection" : true, "depth" : 2.5 * mm, "offsetDistance" : 25 * mm});
        }
        {
            var Q0;
            Q0=makeQuery(id+"F8.opExtrude","CAP_FACE",FACE,{"disambiguationData":[OSD([sQuery(id+"F0.wireOp",EDGE,"E15"),sQuery(id+"F0.wireOp",EDGE,"E23"),sQuery(id+"F0.wireOp",EDGE,"E24"),sQuery(id+"F0.wireOp",EDGE,"E64"),sQuery(id+"F0.wireOp",EDGE,"E65"),sQuery(id+"F0.wireOp",EDGE,"E66"),sQuery(id+"F0.wireOp",EDGE,"E69"),sQuery(id+"F0.wireOp",EDGE,"E70"),sQuery(id+"F7.wireOp",EDGE,"E87")])],"isStart":false});
            var sketch = newSketch(context, id + "F11", { "sketchPlane" : qUnion([Q0])});
            skText(sketch, "E100", { "text": "T.E.S.T.", "fontName": "OpenSans-Regular.ttf"});
            skText(sketch, "E101", { "text": "16 out\n", "fontName": "OpenSans-Regular.ttf"});
            const initialGuessF11  = {"E100": [-0.0225, 0.01848, 1, 0, 0.01], "E101": [-0.01153, 0.03053, 1, 0, 0.006]};
            skSetInitialGuess(sketch, initialGuessF11);
            skSolve(sketch);
        }
        {
            var Q0;
            Q0 = qSketchRegion(id + "F11", true);
            extrude(context, id + "F12", {"entities" : qUnion([Q0]), "operationType" : NewBodyOperationType.REMOVE, "oppositeDirection" : true, "depth" : 5 * mm, "offsetDistance" : 25 * mm});
        }
        {
            var Q0;
            Q0=makeQuery(id+"F3.opExtrude","CAP_FACE",FACE,{"disambiguationData":[OSD([sQuery(id+"F0.wireOp",EDGE,"E25"),sQuery(id+"F0.wireOp",EDGE,"E26"),sQuery(id+"F0.wireOp",EDGE,"E48"),sQuery(id+"F0.wireOp",EDGE,"E49"),sQuery(id+"F0.wireOp",EDGE,"E62"),sQuery(id+"F0.wireOp",EDGE,"E63"),sQuery(id+"F2.wireOp",EDGE,"E76"),sQuery(id+"F2.wireOp",EDGE,"E77")])],"isStart":false});
            var sketch = newSketch(context, id + "F13", { "sketchPlane" : qUnion([Q0])});
            skText(sketch, "E102", { "text": "T.E.S.T.", "fontName": "OpenSans-Regular.ttf"});
            skText(sketch, "E103", { "text": "0 in\n", "fontName": "OpenSans-Regular.ttf"});
            const initialGuessF13  = {"E102": [-0.02292, -0.02673, 1, 0, 0.01], "E103": [-0.00967, -0.0153, 1, 0, 0.006]};
            skSetInitialGuess(sketch, initialGuessF13);
            skSolve(sketch);
        }
        {
            var Q0;
            Q0 = qSketchRegion(id + "F13", true);
            extrude(context, id + "F14", {"entities" : qUnion([Q0]), "operationType" : NewBodyOperationType.REMOVE, "oppositeDirection" : true, "depth" : 5 * mm, "offsetDistance" : 25 * mm});
        }
        {
            var Q0;
            {var subQ0=sQuery(id+"F7.wireOp",EDGE,"E88");var subQ1=sQuery(id+"F0.wireOp",EDGE,"E71");var subQ2=sQuery(id+"F0.wireOp",EDGE,"E0");var subQ3=makeQuery(id+"F0.imprint","INTERSECT",VERTEX,{"disambiguationData":[OD(0.0)],"derivedFrom":[subQ2,subQ1]});var subQ4=sQuery(id+"F0.wireOp",EDGE,"E65");var subQ6=makeQuery(id+"F1.opExtrude","CAP_EDGE",EDGE,{"disambiguationData":[OSD([subQ1]),TDD([makeQuery(id+"F0.imprint","IMPRINT",EDGE,{"disambiguationData":[TD([[makeQuery(id+"F0.imprint","INTERSECT",VERTEX,{"disambiguationData":[OD(0.0)],"derivedFrom":[subQ4,subQ1]}),-1.0]])],"derivedFrom":subQ1}),makeQuery(id+"F0.imprint","IMPRINT",EDGE,{"disambiguationData":[TD([[subQ3,1.0]])],"derivedFrom":subQ1}),makeQuery(id+"F0.imprint","IMPRINT",EDGE,{"disambiguationData":[TD([[makeQuery(id+"F0.imprint","INTERSECT",VERTEX,{"derivedFrom":[subQ1,sQuery(id+"F0.wireOp",EDGE,"E73")]}),1.0]])],"derivedFrom":subQ1})])],"isStart":false});var subQ7=makeQuery(id+"F7.imprint","INTERSECT",VERTEX,{"derivedFrom":[subQ6,subQ0]});Q0=makeQuery(id+"F7.imprint","IMPRINT",FACE,{"disambiguationData":[TD([[makeQuery(id+"F7.imprint","IMPRINT",EDGE,{"disambiguationData":[TD([[subQ7,-1.0]])],"derivedFrom":subQ0}),1.0]])]});}
            extrude(context, id + "F15", {"entities" : qUnion([Q0]), "operationType" : NewBodyOperationType.ADD, "depth" : 15 * mm, "offsetDistance" : 25 * mm});
        }
    });
